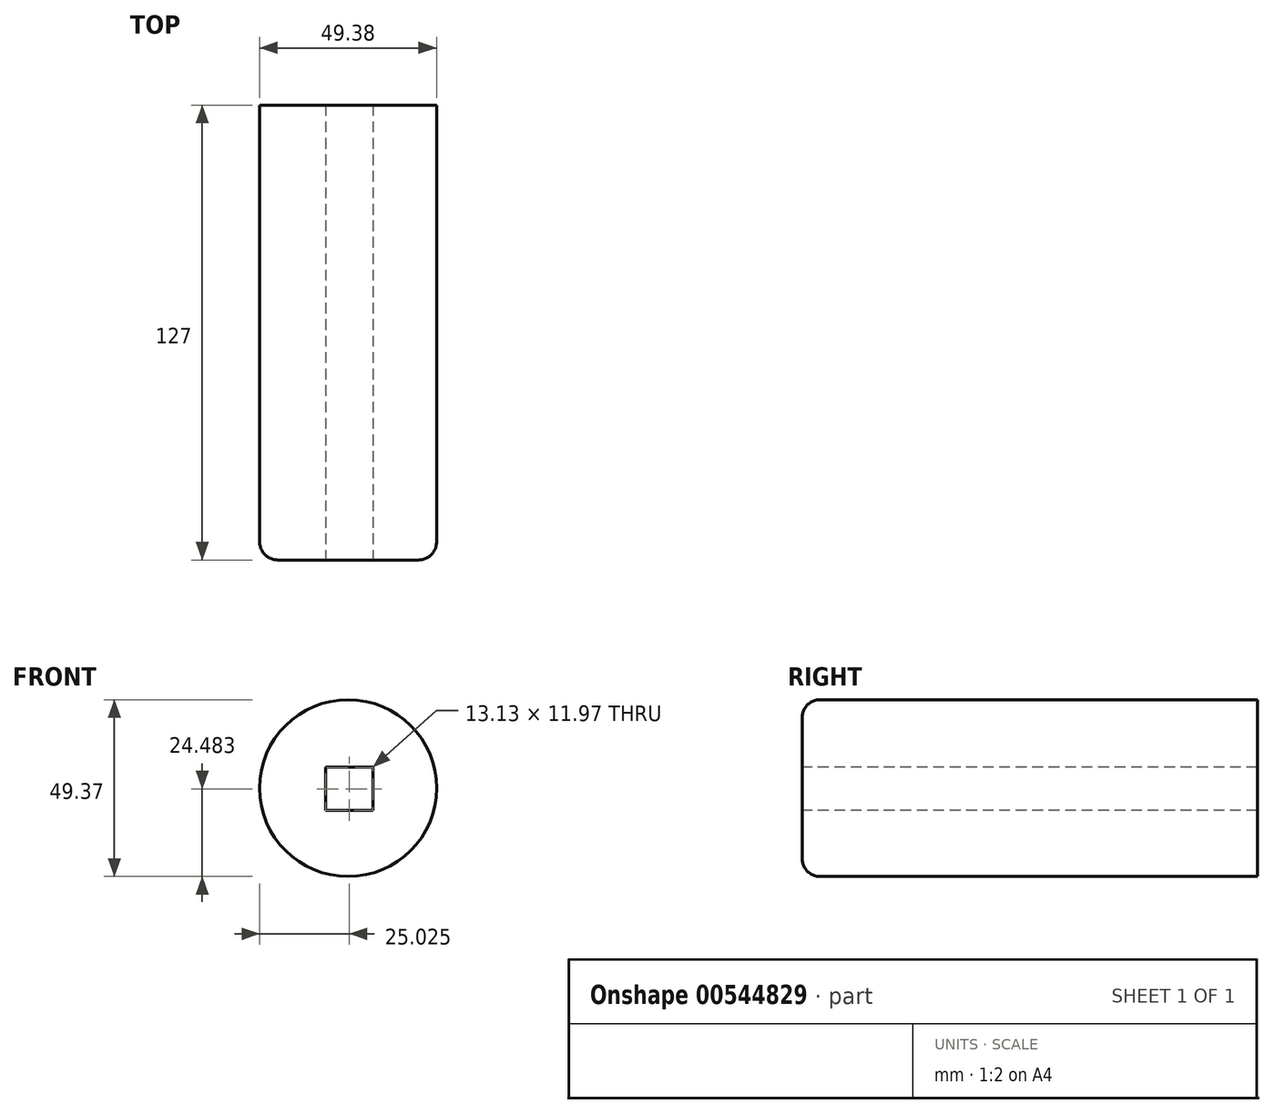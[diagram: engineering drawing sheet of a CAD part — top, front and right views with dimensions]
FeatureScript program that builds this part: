
annotation { "Feature Type Name" : "Feature", "Feature Type Description" : "" }
export const myFeature = defineFeature(function(context is Context, id is Id, definition is map)
    precondition{}
    {
        {
            var Q0;
            Q0=qCreatedBy(makeId("Front.planeOp"),FACE);
            var sketch = newSketch(context, id + "F0", { "sketchPlane" : qUnion([Q0])});
            skCircle(sketch, "E0", {"center": v(-110.14, 36.4) * mm, "radius": 24.69 * mm});
            skSolve(sketch);
        }
        {
            var Q0;
            Q0 = qSketchRegion(id + "F0", true);
            extrude(context, id + "F1", {"entities" : qUnion([Q0]), "depth" : 127 * mm, "offsetDistance" : 25.4 * mm});
        }
        {
            var Q0;
            Q0=makeQuery(id+"F1.opExtrude","CAP_EDGE",EDGE,{"disambiguationData":[OSD([sQuery(id+"F0.wireOp",EDGE,"E0")])],"isStart":false});
            fillet(context, id + "F2", {"entities" : qUnion([Q0]), "radius" : 5.08 * mm, "tangentPropagation" : true, "allowEdgeOverflow" : false});
        }
        {
            var Q0;
            Q0=makeQuery(id+"F1.opExtrude","CAP_FACE",FACE,{"disambiguationData":[OSD([sQuery(id+"F0.wireOp",EDGE,"E0")])],"isStart":false});
            var sketch = newSketch(context, id + "F3", { "sketchPlane" : qUnion([Q0])});
            skLineSegment(sketch, "E1.bottom", {"start": v(-116.37, 42.18) * mm, "end": v(-103.24, 42.18) * mm});
            skLineSegment(sketch, "E1.top", {"start": v(-116.37, 30.2) * mm, "end": v(-103.24, 30.2) * mm});
            skLineSegment(sketch, "E1.left", {"start": v(-116.37, 42.18) * mm, "end": v(-116.37, 30.2) * mm});
            skLineSegment(sketch, "E1.right", {"start": v(-103.24, 42.18) * mm, "end": v(-103.24, 30.2) * mm});
            skSolve(sketch);
        }
        {
            var Q0;
            Q0 = qSketchRegion(id + "F3", true);
            extrude(context, id + "F4", {"entities" : qUnion([Q0]), "operationType" : NewBodyOperationType.REMOVE, "endBound" : BoundingType.THROUGH_ALL, "oppositeDirection" : true, "depth" : 25.4 * mm, "offsetDistance" : 25.4 * mm});
        }
    });
